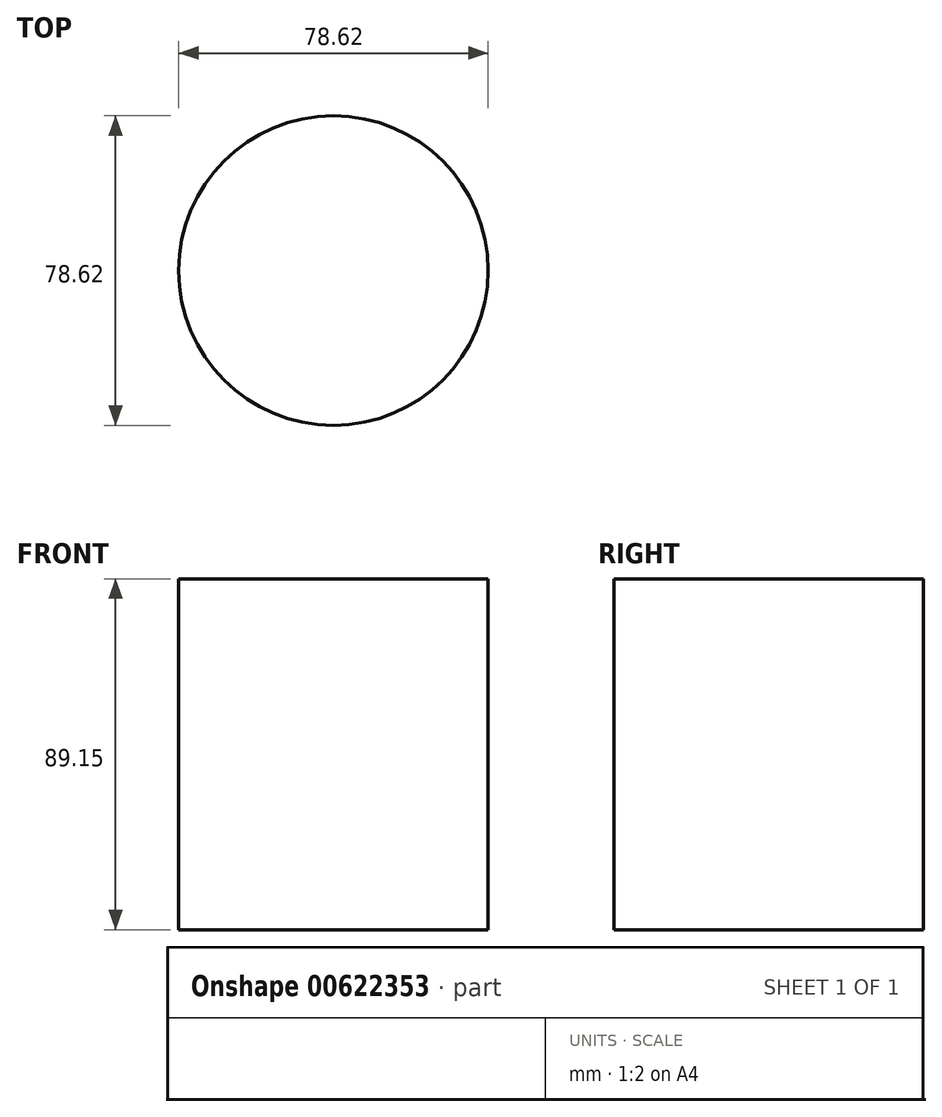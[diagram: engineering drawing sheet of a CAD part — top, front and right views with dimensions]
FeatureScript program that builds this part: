
annotation { "Feature Type Name" : "Feature", "Feature Type Description" : "" }
export const myFeature = defineFeature(function(context is Context, id is Id, definition is map)
    precondition{}
    {
        {
            var Q0;
            Q0=qCreatedBy(makeId("Top.planeOp"),FACE);
            var sketch = newSketch(context, id + "F0", { "sketchPlane" : qUnion([Q0])});
            skCircle(sketch, "E0", {"center": v(0, 0) * mm, "radius": 39.31 * mm});
            skSolve(sketch);
        }
        {
            var Q0;
            Q0=sQuery(id+"F0.wireOp",EDGE,"E0");
            extrude(context, id + "F1", {"bodyType" : ToolBodyType.SURFACE, "surfaceEntities" : qUnion([Q0]), "depth" : 89.15 * mm, "offsetDistance" : 25.4 * mm});
        }
    });
